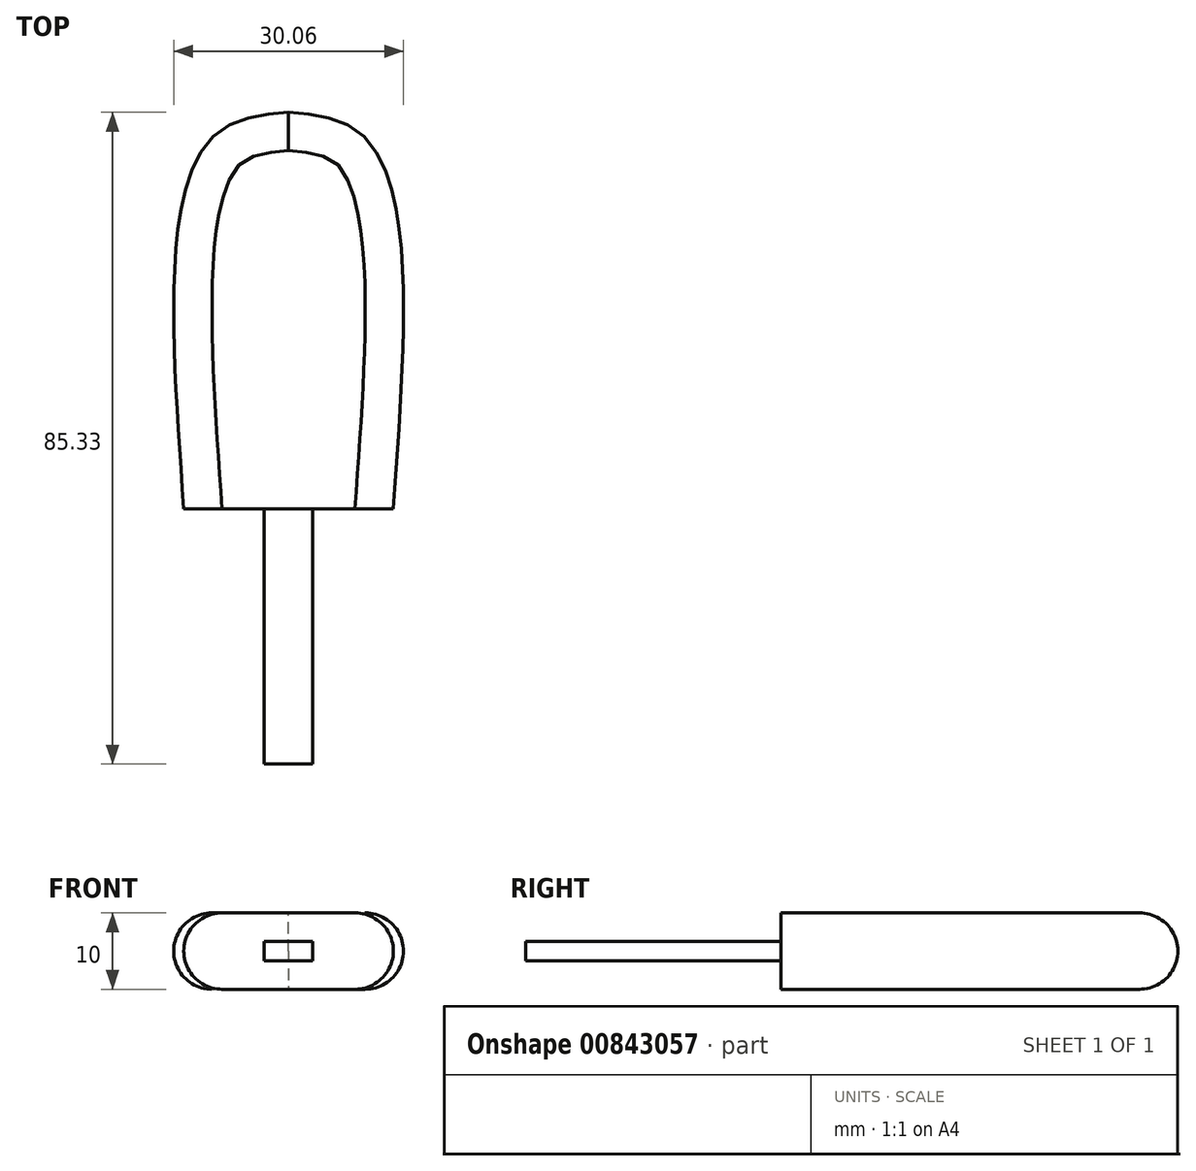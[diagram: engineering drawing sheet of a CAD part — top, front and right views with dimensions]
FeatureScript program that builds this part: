
annotation { "Feature Type Name" : "Feature", "Feature Type Description" : "" }
export const myFeature = defineFeature(function(context is Context, id is Id, definition is map)
    precondition{}
    {
        {
            var Q0;
            Q0=qCreatedBy(makeId("Top.planeOp"),FACE);
            var sketch = newSketch(context, id + "F0", { "sketchPlane" : qUnion([Q0])});
            skFitSpline(sketch, "E0", {"points": [v(-13.7, 0) * mm, v(-14.23, 38.33) * mm, v(-8.73, 49.67) * mm, v(0, 51.9) * mm], "startDerivative": vector(-6.45, 88.82) * mm, "endDerivative": vector(40.3, 3.64) * mm});
            skFitSpline(sketch, "E1.MirrorCS", {"points": [v(13.7, 0) * mm, v(14.23, 38.33) * mm, v(8.73, 49.67) * mm, v(0, 51.9) * mm], "startDerivative": vector(6.45, 88.82) * mm, "endDerivative": vector(-40.3, 3.64) * mm});
            skLineSegment(sketch, "E2", {"start": v(-13.7, 0) * mm, "end": v(13.7, 0) * mm});
            skSolve(sketch);
        }
        {
            var Q0;
            Q0=makeQuery(id+"F0.imprint","IMPRINT",FACE,{"disambiguationData":[TD([[makeQuery(id+"F0.imprint","IMPRINT",EDGE,{"derivedFrom":sQuery(id+"F0.wireOp",EDGE,"E0")}),-1.0]])]});
            extrude(context, id + "F1", {"entities" : qUnion([Q0]), "endBound" : BoundingType.SYMMETRIC, "depth" : 10 * mm, "offsetDistance" : 25 * mm});
        }
        {
            var Q0;
            Q0=makeQuery(id+"F1.opExtrude","CAP_EDGE",EDGE,{"disambiguationData":[OSD([sQuery(id+"F0.wireOp",EDGE,"E0")])],"isStart":false});
            var Q1;
            Q1=makeQuery(id+"F1.opExtrude","CAP_EDGE",EDGE,{"disambiguationData":[OSD([sQuery(id+"F0.wireOp",EDGE,"E1.MirrorCS")])],"isStart":false});
            var Q2;
            Q2=makeQuery(id+"F1.opExtrude","CAP_EDGE",EDGE,{"disambiguationData":[OSD([sQuery(id+"F0.wireOp",EDGE,"E0")])],"isStart":true});
            var Q3;
            Q3=makeQuery(id+"F1.opExtrude","CAP_EDGE",EDGE,{"disambiguationData":[OSD([sQuery(id+"F0.wireOp",EDGE,"E1.MirrorCS")])],"isStart":true});
            fillet(context, id + "F2", {"entities" : qUnion([Q0, Q1, Q2, Q3]), "radius" : 5 * mm, "tangentPropagation" : true, "allowEdgeOverflow" : false});
        }
        {
            var Q0;
            Q0=qCreatedBy(makeId("Top.planeOp"),FACE);
            var sketch = newSketch(context, id + "F3", { "sketchPlane" : qUnion([Q0])});
            skLineSegment(sketch, "E3", {"start": v(0, 15.9) * mm, "end": v(-3.18, 15.9) * mm});
            skLineSegment(sketch, "E4", {"start": v(-3.18, 15.9) * mm, "end": v(-3.18, -33.43) * mm});
            skLineSegment(sketch, "E5", {"start": v(-3.18, -33.43) * mm, "end": v(0, -33.43) * mm});
            skLineSegment(sketch, "E6.MirrorCS", {"start": v(3.18, 15.9) * mm, "end": v(3.18, -33.43) * mm});
            skLineSegment(sketch, "E7.MirrorCS", {"start": v(0, 15.9) * mm, "end": v(3.18, 15.9) * mm});
            skLineSegment(sketch, "E8.MirrorCS", {"start": v(3.18, -33.43) * mm, "end": v(0, -33.43) * mm});
            skSolve(sketch);
        }
        {
            var Q0;
            Q0 = qSketchRegion(id + "F3", true);
            extrude(context, id + "F4", {"entities" : qUnion([Q0]), "operationType" : NewBodyOperationType.ADD, "endBound" : BoundingType.SYMMETRIC, "depth" : 2.5 * mm, "offsetDistance" : 25 * mm});
        }
    });
